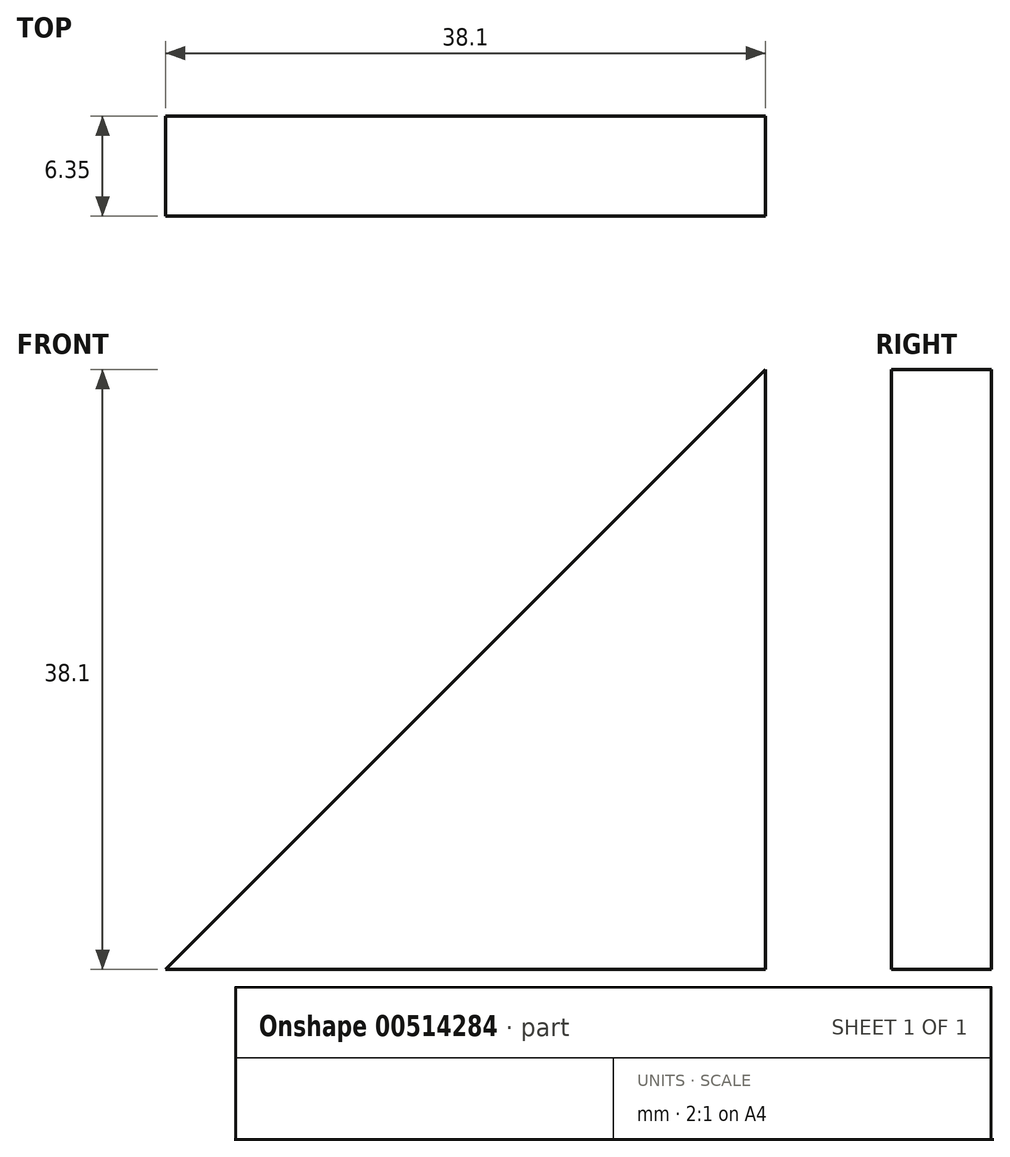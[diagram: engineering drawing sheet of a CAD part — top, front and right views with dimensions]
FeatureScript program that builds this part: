
annotation { "Feature Type Name" : "Feature", "Feature Type Description" : "" }
export const myFeature = defineFeature(function(context is Context, id is Id, definition is map)
    precondition{}
    {
        {
            var Q0;
            Q0=qCreatedBy(makeId("Front.planeOp"),FACE);
            var sketch = newSketch(context, id + "F0", { "sketchPlane" : qUnion([Q0])});
            skLineSegment(sketch, "E0", {"start": v(0, 0) * mm, "end": v(-38.1, 0) * mm});
            skLineSegment(sketch, "E1", {"start": v(-38.1, 0) * mm, "end": v(0, 38.1) * mm});
            skLineSegment(sketch, "E2", {"start": v(0, 38.1) * mm, "end": v(0, 0) * mm});
            skSolve(sketch);
        }
        {
            var Q0;
            Q0 = qSketchRegion(id + "F0", true);
            extrude(context, id + "F1", {"entities" : qUnion([Q0]), "depth" : 6.35 * mm});
        }
    });
